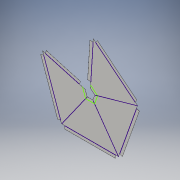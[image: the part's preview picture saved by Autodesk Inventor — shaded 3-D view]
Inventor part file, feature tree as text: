
AUTODESK INVENTOR PART (.ipt)
format: ipt  version: 2016 (Build 200138000, 138)  size: 202,752 bytes
history: native  units: in
note: dims shown in document units (in); Inventor stores cm internally (conversion verified against a paired STEP export)
features: sketch x3, extrude x2
ambient origin geometry x8: Origin, YZ Plane, XZ Plane, XY Plane, X Axis, Y Axis, Z Axis, Center Point
bodies: Body1 (feature_tree)
feature tree (5):
  extrude  "Extrusion2"  Depth=3.7402in
  extrude  "Extrusion3"  Depth=2.227in
  sketch  "Sketch3"  dims[d4=2.7276in d16=0.591in d17=0.591in d18=0.591in d19=3.74in d20=2.728in d21=3.74in d22=2.728in d23=3.74in d24=2.728in d25=0.005in d26=0.0in d34=0.2in d35=0.2in d38=0.2in d39=0.2in d42=0.2in d43=0.2in d46=0.2in d47=0.2in d50=0.2in d51=0.2in d56=0.2in d58=0.2in d64=0.3761in d65=0.15in d66=0.3761in d67=0.15in d68=0.3761in d69=0.15in d70=0.3761in d71=0.15in d72=0.3761in d73=0.15in d74=0.005in d75=0.0in d76=0.2in]
  sketch  "Sketch1"  dims[d0=2.7276in d1=3.7402in]
  sketch  "Sketch2"  dims[d2=0.5906in d3=2.227in]
